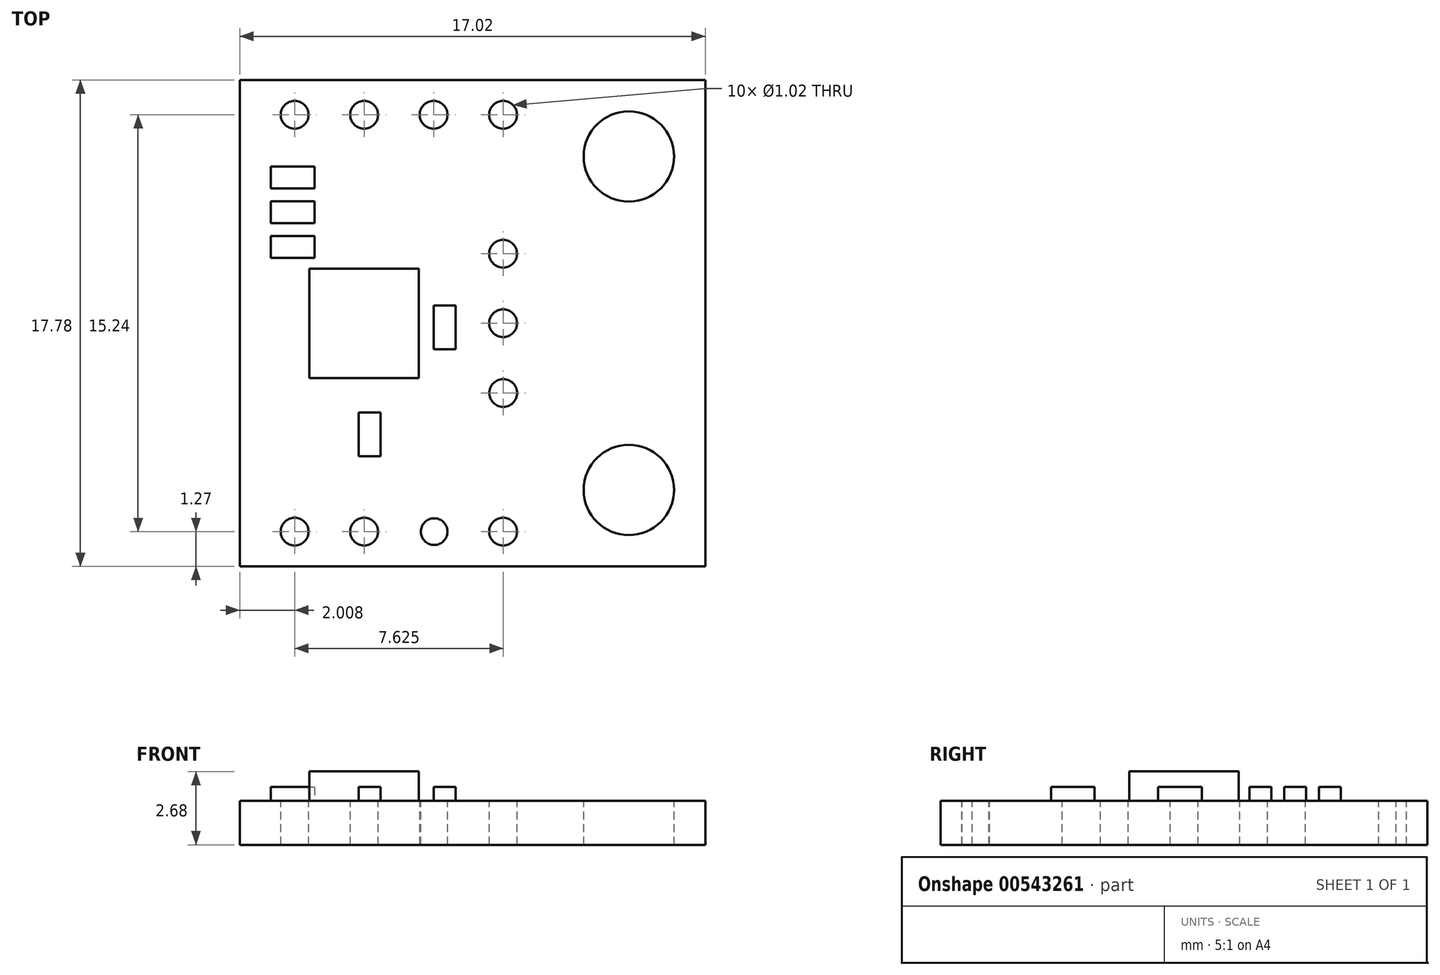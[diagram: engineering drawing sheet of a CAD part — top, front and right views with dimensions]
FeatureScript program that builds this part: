
annotation { "Feature Type Name" : "Feature", "Feature Type Description" : "" }
export const myFeature = defineFeature(function(context is Context, id is Id, definition is map)
    precondition{}
    {
        {
            var Q0;
            Q0=qCreatedBy(makeId("Top.planeOp"),FACE);
            var sketch = newSketch(context, id + "F0", { "sketchPlane" : qUnion([Q0])});
            skLineSegment(sketch, "E0.bottom", {"start": v(-8.5, 8.9) * mm, "end": v(8.5, 8.9) * mm});
            skLineSegment(sketch, "E0.top", {"start": v(-8.5, -8.9) * mm, "end": v(8.5, -8.9) * mm});
            skLineSegment(sketch, "E0.left", {"start": v(-8.5, 8.9) * mm, "end": v(-8.5, -8.9) * mm});
            skLineSegment(sketch, "E0.right", {"start": v(8.5, 8.9) * mm, "end": v(8.5, -8.9) * mm});
            skSolve(sketch);
        }
        {
            var Q0;
            Q0 = qSketchRegion(id + "F0", true);
            extrude(context, id + "F1", {"entities" : qUnion([Q0]), "depth" : 0.26 * mm, "offsetDistance" : 25 * mm});
        }
        {
            var Q0;
            Q0 = qSketchRegion(id + "F0", true);
            extrude(context, id + "F2", {"entities" : qUnion([Q0]), "operationType" : NewBodyOperationType.ADD, "oppositeDirection" : true, "depth" : 1.35 * mm, "offsetDistance" : 25 * mm});
        }
        {
            var Q0;
            Q0=makeQuery(id+"F1.opExtrude","CAP_FACE",FACE,{"disambiguationData":[OSD([sQuery(id+"F0.wireOp",EDGE,"E0.bottom"),sQuery(id+"F0.wireOp",EDGE,"E0.top"),sQuery(id+"F0.wireOp",EDGE,"E0.left"),sQuery(id+"F0.wireOp",EDGE,"E0.right")])],"isStart":false});
            var sketch = newSketch(context, id + "F3", { "sketchPlane" : qUnion([Q0])});
            skLineSegment(sketch, "E1", {"start": v(5.71, 7.75) * mm, "end": v(5.71, 4.45) * mm, "construction": true});
            skLineSegment(sketch, "E2", {"start": v(4.06, 6.1) * mm, "end": v(7.37, 6.1) * mm, "construction": true});
            skCircle(sketch, "E3", {"center": v(5.72, 6.1) * mm, "radius": 1.65 * mm});
            skLineSegment(sketch, "E4", {"start": v(5.71, -7.75) * mm, "end": v(5.71, -4.45) * mm, "construction": true});
            skLineSegment(sketch, "E5", {"start": v(7.37, -6.1) * mm, "end": v(4.06, -6.1) * mm, "construction": true});
            skCircle(sketch, "E6", {"center": v(5.72, -6.1) * mm, "radius": 1.65 * mm});
            skLineSegment(sketch, "E7", {"start": v(-1.4, -7.13) * mm, "end": v(-1.4, -8.1) * mm, "construction": true});
            skLineSegment(sketch, "E8", {"start": v(-1.89, -7.62) * mm, "end": v(-0.91, -7.62) * mm, "construction": true});
            skCircle(sketch, "E9", {"center": v(-1.4, -7.62) * mm, "radius": 0.49 * mm});
            skCircle(sketch, "E10", {"center": v(1.12, -7.62) * mm, "radius": 0.5 * mm});
            skPoint(sketch, "E10.first.point", {"position": v(1.12, -7.11) * mm});
            skPoint(sketch, "E10.second.point", {"position": v(1.12, -8.13) * mm});
            skPoint(sketch, "E10.third.point", {"position": v(1.48, -7.98) * mm});
            skCircle(sketch, "E11", {"center": v(-3.96, -7.62) * mm, "radius": 0.5 * mm});
            skPoint(sketch, "E11.first.point", {"position": v(-4.1, -7.13) * mm});
            skPoint(sketch, "E11.second.point", {"position": v(-4.32, -7.98) * mm});
            skPoint(sketch, "E11.third.point", {"position": v(-3.6, -7.98) * mm});
            skCircle(sketch, "E12", {"center": v(-6.5, -7.62) * mm, "radius": 0.5 * mm});
            skPoint(sketch, "E12.first.point", {"position": v(-7, -7.62) * mm});
            skPoint(sketch, "E12.second.point", {"position": v(-6.14, -7.98) * mm});
            skPoint(sketch, "E12.third.point", {"position": v(-6.5, -7.11) * mm});
            skCircle(sketch, "E13", {"center": v(1.12, -2.55) * mm, "radius": 0.5 * mm});
            skPoint(sketch, "E13.first.point", {"position": v(0.63, -2.7) * mm});
            skPoint(sketch, "E13.second.point", {"position": v(1.39, -2.99) * mm});
            skPoint(sketch, "E13.third.point", {"position": v(1.11, -2.04) * mm});
            skCircle(sketch, "E14", {"center": v(1.12, 0) * mm, "radius": 0.5 * mm});
            skPoint(sketch, "E14.first.point", {"position": v(0.68, 0.25) * mm});
            skPoint(sketch, "E14.second.point", {"position": v(1.25, -0.5) * mm});
            skPoint(sketch, "E14.third.point", {"position": v(1.37, 0.44) * mm});
            skCircle(sketch, "E15", {"center": v(1.12, 2.54) * mm, "radius": 0.5 * mm});
            skPoint(sketch, "E15.first.point", {"position": v(0.68, 2.29) * mm});
            skPoint(sketch, "E15.second.point", {"position": v(1.48, 2.18) * mm});
            skPoint(sketch, "E15.third.point", {"position": v(1.12, 3.05) * mm});
            skCircle(sketch, "E16", {"center": v(1.12, 7.62) * mm, "radius": 0.5 * mm});
            skPoint(sketch, "E16.first.point", {"position": v(0.76, 7.98) * mm});
            skPoint(sketch, "E16.second.point", {"position": v(0.76, 7.26) * mm});
            skPoint(sketch, "E16.third.point", {"position": v(1.63, 7.62) * mm});
            skCircle(sketch, "E17", {"center": v(-1.42, 7.62) * mm, "radius": 0.5 * mm});
            skPoint(sketch, "E17.first.point", {"position": v(-1.91, 7.75) * mm});
            skPoint(sketch, "E17.second.point", {"position": v(-1.17, 7.18) * mm});
            skPoint(sketch, "E17.third.point", {"position": v(-1.06, 7.98) * mm});
            skCircle(sketch, "E18", {"center": v(-3.96, 7.62) * mm, "radius": 0.5 * mm});
            skPoint(sketch, "E18.first.point", {"position": v(-4.45, 7.49) * mm});
            skPoint(sketch, "E18.second.point", {"position": v(-3.83, 7.13) * mm});
            skPoint(sketch, "E18.third.point", {"position": v(-3.7, 8.06) * mm});
            skCircle(sketch, "E19", {"center": v(-6.5, 7.62) * mm, "radius": 0.5 * mm});
            skPoint(sketch, "E19.first.point", {"position": v(-6.86, 7.98) * mm});
            skPoint(sketch, "E19.second.point", {"position": v(-6.76, 7.18) * mm});
            skPoint(sketch, "E19.third.point", {"position": v(-6, 7.62) * mm});
            skSolve(sketch);
        }
        {
            var Q0;
            Q0=makeQuery(id+"F3.imprint","IMPRINT",FACE,{"disambiguationData":[TD([[makeQuery(id+"F3.imprint","IMPRINT",EDGE,{"derivedFrom":sQuery(id+"F3.wireOp",EDGE,"E19")}),1.0]])]});
            var Q1;
            Q1=makeQuery(id+"F3.imprint","IMPRINT",FACE,{"disambiguationData":[TD([[makeQuery(id+"F3.imprint","IMPRINT",EDGE,{"derivedFrom":sQuery(id+"F3.wireOp",EDGE,"E18")}),1.0]])]});
            var Q2;
            Q2=makeQuery(id+"F3.imprint","IMPRINT",FACE,{"disambiguationData":[TD([[makeQuery(id+"F3.imprint","IMPRINT",EDGE,{"derivedFrom":sQuery(id+"F3.wireOp",EDGE,"E17")}),1.0]])]});
            var Q3;
            Q3=makeQuery(id+"F3.imprint","IMPRINT",FACE,{"disambiguationData":[TD([[makeQuery(id+"F3.imprint","IMPRINT",EDGE,{"derivedFrom":sQuery(id+"F3.wireOp",EDGE,"E16")}),1.0]])]});
            var Q4;
            Q4=makeQuery(id+"F3.imprint","IMPRINT",FACE,{"disambiguationData":[TD([[makeQuery(id+"F3.imprint","IMPRINT",EDGE,{"derivedFrom":sQuery(id+"F3.wireOp",EDGE,"E15")}),1.0]])]});
            var Q5;
            Q5=makeQuery(id+"F3.imprint","IMPRINT",FACE,{"disambiguationData":[TD([[makeQuery(id+"F3.imprint","IMPRINT",EDGE,{"derivedFrom":sQuery(id+"F3.wireOp",EDGE,"E14")}),1.0]])]});
            var Q6;
            Q6=makeQuery(id+"F3.imprint","IMPRINT",FACE,{"disambiguationData":[TD([[makeQuery(id+"F3.imprint","IMPRINT",EDGE,{"derivedFrom":sQuery(id+"F3.wireOp",EDGE,"E13")}),1.0]])]});
            var Q7;
            Q7=makeQuery(id+"F3.imprint","IMPRINT",FACE,{"disambiguationData":[TD([[makeQuery(id+"F3.imprint","IMPRINT",EDGE,{"derivedFrom":sQuery(id+"F3.wireOp",EDGE,"E10")}),1.0]])]});
            var Q8;
            Q8=makeQuery(id+"F3.imprint","IMPRINT",FACE,{"disambiguationData":[TD([[makeQuery(id+"F3.imprint","IMPRINT",EDGE,{"derivedFrom":sQuery(id+"F3.wireOp",EDGE,"E9")}),1.0]])]});
            var Q9;
            Q9=makeQuery(id+"F3.imprint","IMPRINT",FACE,{"disambiguationData":[TD([[makeQuery(id+"F3.imprint","IMPRINT",EDGE,{"derivedFrom":sQuery(id+"F3.wireOp",EDGE,"E11")}),1.0]])]});
            var Q10;
            Q10=makeQuery(id+"F3.imprint","IMPRINT",FACE,{"disambiguationData":[TD([[makeQuery(id+"F3.imprint","IMPRINT",EDGE,{"derivedFrom":sQuery(id+"F3.wireOp",EDGE,"E12")}),1.0]])]});
            var Q11;
            Q11=makeQuery(id+"F3.imprint","IMPRINT",FACE,{"disambiguationData":[TD([[makeQuery(id+"F3.imprint","IMPRINT",EDGE,{"derivedFrom":sQuery(id+"F3.wireOp",EDGE,"E6")}),1.0]])]});
            var Q12;
            Q12=makeQuery(id+"F3.imprint","IMPRINT",FACE,{"disambiguationData":[TD([[makeQuery(id+"F3.imprint","IMPRINT",EDGE,{"derivedFrom":sQuery(id+"F3.wireOp",EDGE,"E3")}),1.0]])]});
            var Q13;
            Q13=makeQuery(id+"F2.opExtrude","CAP_FACE",FACE,{"disambiguationData":[OSD([sQuery(id+"F0.wireOp",EDGE,"E0.bottom"),sQuery(id+"F0.wireOp",EDGE,"E0.top"),sQuery(id+"F0.wireOp",EDGE,"E0.left"),sQuery(id+"F0.wireOp",EDGE,"E0.right")])],"isStart":false});
            extrude(context, id + "F4", {"entities" : qUnion([Q0, Q1, Q2, Q3, Q4, Q5, Q6, Q7, Q8, Q9, Q10, Q11, Q12]), "operationType" : NewBodyOperationType.REMOVE, "endBound" : BoundingType.UP_TO_SURFACE, "oppositeDirection" : true, "depth" : 25 * mm, "endBoundEntityFace" : qUnion([Q13]), "offsetDistance" : 25 * mm});
        }
        {
            var Q0;
            Q0=makeQuery(id+"F1.opExtrude","CAP_FACE",FACE,{"disambiguationData":[OSD([sQuery(id+"F0.wireOp",EDGE,"E0.bottom"),sQuery(id+"F0.wireOp",EDGE,"E0.top"),sQuery(id+"F0.wireOp",EDGE,"E0.left"),sQuery(id+"F0.wireOp",EDGE,"E0.right")])],"isStart":false});
            var sketch = newSketch(context, id + "F5", { "sketchPlane" : qUnion([Q0])});
            skLineSegment(sketch, "E20.bottom", {"start": v(-7.38, 5.73) * mm, "end": v(-5.78, 5.73) * mm});
            skLineSegment(sketch, "E20.top", {"start": v(-7.38, 4.93) * mm, "end": v(-5.78, 4.93) * mm});
            skLineSegment(sketch, "E20.left", {"start": v(-7.38, 5.73) * mm, "end": v(-7.38, 4.93) * mm});
            skLineSegment(sketch, "E20.right", {"start": v(-5.78, 5.73) * mm, "end": v(-5.78, 4.93) * mm});
            skLineSegment(sketch, "E21.bottom", {"start": v(-7.38, 4.46) * mm, "end": v(-5.78, 4.46) * mm});
            skLineSegment(sketch, "E21.top", {"start": v(-7.38, 3.66) * mm, "end": v(-5.78, 3.66) * mm});
            skLineSegment(sketch, "E21.left", {"start": v(-7.38, 4.46) * mm, "end": v(-7.38, 3.66) * mm});
            skLineSegment(sketch, "E21.right", {"start": v(-5.78, 4.46) * mm, "end": v(-5.78, 3.66) * mm});
            skLineSegment(sketch, "E22.bottom", {"start": v(-7.38, 3.2) * mm, "end": v(-5.78, 3.2) * mm});
            skLineSegment(sketch, "E22.top", {"start": v(-7.38, 2.4) * mm, "end": v(-5.78, 2.4) * mm});
            skLineSegment(sketch, "E22.left", {"start": v(-7.38, 3.2) * mm, "end": v(-7.38, 2.4) * mm});
            skLineSegment(sketch, "E22.right", {"start": v(-5.78, 3.2) * mm, "end": v(-5.78, 2.4) * mm});
            skLineSegment(sketch, "E23.bottom", {"start": v(-1.42, 0.65) * mm, "end": v(-0.62, 0.65) * mm});
            skLineSegment(sketch, "E23.top", {"start": v(-1.42, -0.95) * mm, "end": v(-0.62, -0.95) * mm});
            skLineSegment(sketch, "E23.left", {"start": v(-1.42, 0.65) * mm, "end": v(-1.42, -0.95) * mm});
            skLineSegment(sketch, "E23.right", {"start": v(-0.62, 0.65) * mm, "end": v(-0.62, -0.95) * mm});
            skLineSegment(sketch, "E24.bottom", {"start": v(-4.16, -3.26) * mm, "end": v(-3.36, -3.26) * mm});
            skLineSegment(sketch, "E24.top", {"start": v(-4.16, -4.86) * mm, "end": v(-3.36, -4.86) * mm});
            skLineSegment(sketch, "E24.left", {"start": v(-4.16, -3.26) * mm, "end": v(-4.16, -4.86) * mm});
            skLineSegment(sketch, "E24.right", {"start": v(-3.36, -3.26) * mm, "end": v(-3.36, -4.86) * mm});
            skSolve(sketch);
        }
        {
            var Q0;
            Q0 = qSketchRegion(id + "F5", true);
            extrude(context, id + "F6", {"entities" : qUnion([Q0]), "operationType" : NewBodyOperationType.ADD, "depth" : 0.5 * mm, "offsetDistance" : 25 * mm});
        }
        {
            var Q0;
            Q0=makeQuery(id+"F1.opExtrude","CAP_FACE",FACE,{"disambiguationData":[OSD([sQuery(id+"F0.wireOp",EDGE,"E0.bottom"),sQuery(id+"F0.wireOp",EDGE,"E0.top"),sQuery(id+"F0.wireOp",EDGE,"E0.left"),sQuery(id+"F0.wireOp",EDGE,"E0.right")])],"isStart":false});
            var sketch = newSketch(context, id + "F7", { "sketchPlane" : qUnion([Q0])});
            skLineSegment(sketch, "E25.bottom", {"start": v(-5.96, 2) * mm, "end": v(-1.96, 2) * mm});
            skLineSegment(sketch, "E25.top", {"start": v(-5.96, -2) * mm, "end": v(-1.96, -2) * mm});
            skLineSegment(sketch, "E25.left", {"start": v(-5.96, 2) * mm, "end": v(-5.96, -2) * mm});
            skLineSegment(sketch, "E25.right", {"start": v(-1.96, 2) * mm, "end": v(-1.96, -2) * mm});
            skSolve(sketch);
        }
        {
            var Q0;
            Q0 = qSketchRegion(id + "F7", true);
            extrude(context, id + "F8", {"entities" : qUnion([Q0]), "operationType" : NewBodyOperationType.ADD, "depth" : 1.07 * mm, "offsetDistance" : 25 * mm});
        }
    });
